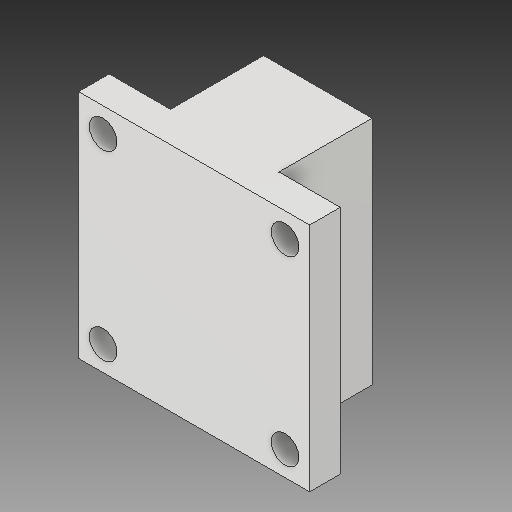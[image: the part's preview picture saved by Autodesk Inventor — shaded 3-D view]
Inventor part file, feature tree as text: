
AUTODESK INVENTOR PART (.ipt)
format: ipt  version: 2019.3 (Build 233278000, 278)  size: 146,432 bytes
history: native  units: mm
features: extrude x3, sketch x3, other x3, reference x2
ambient origin geometry x8: Origin, YZ Plane, XZ Plane, XY Plane, X Axis, Y Axis, Z Axis, Center Point
bodies: Solid1 (feature_tree)
feature tree (11):
  extrude  "Extrusion1"  Depth=10.0mm TaperAngle=0.0deg
  extrude  "Extrusion2"  Depth=25.0mm
  extrude  "Extrusion4"  Depth=35.4mm
  sketch  "Sketch1"  dims[d0=25.0mm d4=10.0mm d5=0.0mm]
  reference  "Reference1"
  reference  "Reference2"
  sketch  "Sketch3"  dims[d19=30.4mm d20=0.0mm d31=25.0mm]
  sketch  "Sketch5"  dims[d32=5.0mm d33=9.0mm d34=9.0mm d35=9.0mm d36=9.0mm d37=8.0mm d38=8.0mm d39=8.0mm d40=8.0mm d41=8.0mm d42=8.0mm d43=8.0mm d44=8.0mm d45=35.4mm d46=20.0mm d47=5.0mm d48=5.0mm d49=25.4mm d50=25.4mm d51=35.4mm d52=0.0mm]
  parser-record x1  (decoder bookkeeping rows leaked as tree rows — omitted from the tree; the rows remain in map.json)
  other  "Assembly.iam"
  other  "LateralBars:1"
note: 1 file-system path scrubbed to <path> (originals preserved in map.json)
